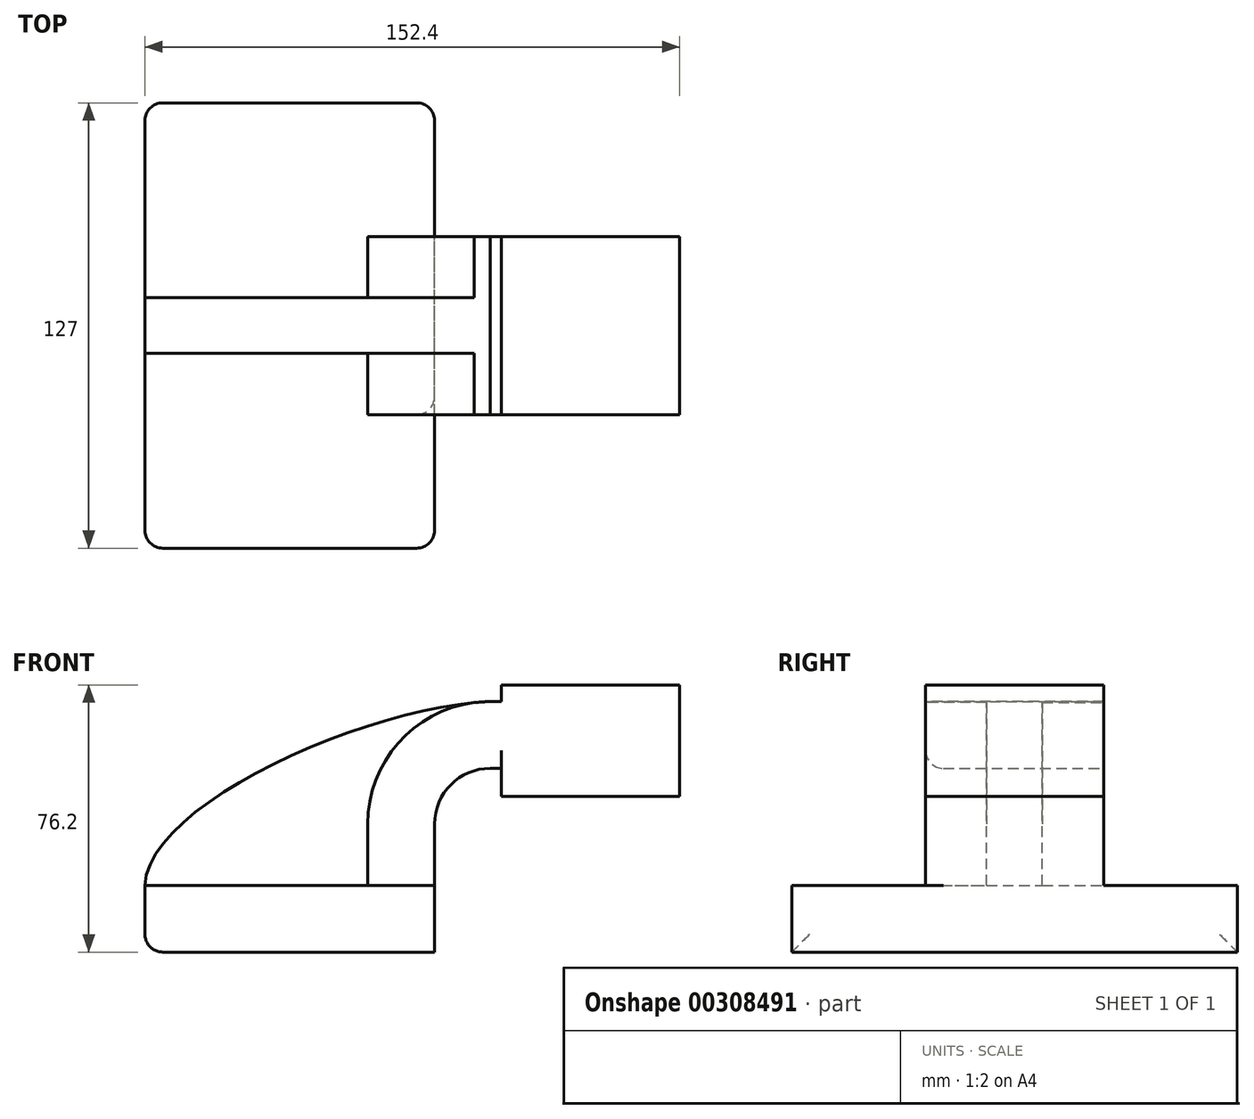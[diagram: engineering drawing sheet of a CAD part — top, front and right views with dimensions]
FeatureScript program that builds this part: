
annotation { "Feature Type Name" : "Feature", "Feature Type Description" : "" }
export const myFeature = defineFeature(function(context is Context, id is Id, definition is map)
    precondition{}
    {
        {
            var Q0;
            Q0=qCreatedBy(makeId("Front.planeOp"),FACE);
            var sketch = newSketch(context, id + "F0", { "sketchPlane" : qUnion([Q0])});
            skLineSegment(sketch, "E0.bottom", {"start": v(41.28, -9.52) * mm, "end": v(-41.28, -9.53) * mm});
            skLineSegment(sketch, "E0.top", {"start": v(41.27, 9.53) * mm, "end": v(-41.28, 9.53) * mm});
            skLineSegment(sketch, "E0.left", {"start": v(41.28, -9.52) * mm, "end": v(41.28, 9.53) * mm});
            skLineSegment(sketch, "E0.right", {"start": v(-41.28, -9.53) * mm, "end": v(-41.28, 9.53) * mm});
            skPoint(sketch, "E0.middle", {"position": v(0, 0) * mm});
            skLineSegment(sketch, "E1.bottom", {"start": v(60.32, 34.93) * mm, "end": v(111.12, 34.93) * mm});
            skLineSegment(sketch, "E1.top", {"start": v(60.32, 66.68) * mm, "end": v(111.12, 66.68) * mm});
            skLineSegment(sketch, "E1.left", {"start": v(60.32, 34.93) * mm, "end": v(60.32, 66.68) * mm});
            skLineSegment(sketch, "E1.right", {"start": v(111.12, 34.93) * mm, "end": v(111.12, 66.68) * mm});
            skPoint(sketch, "E1.middle", {"position": v(85.72, 50.8) * mm});
            skLineSegment(sketch, "E2", {"start": v(41.27, 9.53) * mm, "end": v(41.27, 27) * mm});
            skArc(sketch, "E3", {"start": v(41.27, 27) * mm, "mid": v(45.92, 38.23) * mm, "end": v(57.15, 42.88) * mm});
            skLineSegment(sketch, "E4", {"start": v(57.15, 42.88) * mm, "end": v(110.29, 42.88) * mm});
            skLineSegment(sketch, "E5.0", {"start": v(57.15, 61.93) * mm, "end": v(110.29, 61.93) * mm});
            skArc(sketch, "E5.1", {"start": v(22.23, 27) * mm, "mid": v(32.45, 51.7) * mm, "end": v(57.15, 61.93) * mm});
            skLineSegment(sketch, "E5.2", {"start": v(22.23, 9.53) * mm, "end": v(22.23, 27) * mm});
            skLineSegment(sketch, "E6", {"start": v(110.29, 42.88) * mm, "end": v(110.29, 61.93) * mm});
            skFitSpline(sketch, "E7", {"points": [v(-41.28, 9.53) * mm, v(57.15, 61.93) * mm], "startDerivative": vector(2.65, 70.47) * mm, "endDerivative": vector(102.94, 3.6) * mm});
            skLineSegment(sketch, "E8", {"start": v(111.12, 66.68) * mm, "end": v(111.12, 34.93) * mm});
            skSolve(sketch);
        }
        {
            var Q0;
            Q0=makeQuery(id+"F0.imprint","IMPRINT",FACE,{"disambiguationData":[TD([[makeQuery(id+"F0.imprint","IMPRINT",EDGE,{"derivedFrom":sQuery(id+"F0.wireOp",EDGE,"E0.bottom")}),-1.0]])]});
            extrude(context, id + "F1", {"entities" : qUnion([Q0]), "endBound" : BoundingType.SYMMETRIC, "depth" : 127 * mm});
        }
        {
            var Q0;
            {var subQ1=sQuery(id+"F0.wireOp",EDGE,"E2");Q0=makeQuery(id+"F0.imprint","IMPRINT",FACE,{"disambiguationData":[TD([[makeQuery(id+"F0.imprint","IMPRINT",EDGE,{"derivedFrom":subQ1}),1.0]])]});}
            var Q1;
            {var subQ5=sQuery(id+"F0.wireOp",EDGE,"E6");Q1=makeQuery(id+"F0.imprint","IMPRINT",FACE,{"disambiguationData":[TD([[makeQuery(id+"F0.imprint","IMPRINT",EDGE,{"derivedFrom":subQ5}),1.0]])]});}
            var Q2;
            {var subQ5=sQuery(id+"F0.wireOp",EDGE,"E1.bottom");Q2=makeQuery(id+"F0.imprint","IMPRINT",FACE,{"disambiguationData":[TD([[makeQuery(id+"F0.imprint","IMPRINT",EDGE,{"derivedFrom":subQ5}),1.0]])]});}
            extrude(context, id + "F2", {"entities" : qUnion([Q0, Q1, Q2]), "operationType" : NewBodyOperationType.ADD, "endBound" : BoundingType.SYMMETRIC, "depth" : 50.8 * mm});
        }
        {
            var Q0;
            {var subQ3=sQuery(id+"F0.wireOp",EDGE,"E5.2");Q0=makeQuery(id+"F0.imprint","IMPRINT",FACE,{"disambiguationData":[TD([[makeQuery(id+"F0.imprint","IMPRINT",EDGE,{"derivedFrom":subQ3}),1.0]])]});}
            extrude(context, id + "F3", {"entities" : qUnion([Q0]), "operationType" : NewBodyOperationType.ADD, "endBound" : BoundingType.SYMMETRIC, "depth" : 15.88 * mm});
        }
        {
            var Q0;
            Q0=makeQuery(id+"F1.opExtrude","CAP_EDGE",EDGE,{"disambiguationData":[OSD([sQuery(id+"F0.wireOp",EDGE,"E0.left")])],"isStart":false});
            var Q1;
            Q1=makeQuery(id+"F1.opExtrude","CAP_EDGE",EDGE,{"disambiguationData":[OSD([sQuery(id+"F0.wireOp",EDGE,"E0.left")])],"isStart":true});
            var Q2;
            Q2=makeQuery(id+"F2.opExtrude","CAP_EDGE",EDGE,{"disambiguationData":[OSD([sQuery(id+"F0.wireOp",EDGE,"E4")])],"isStart":false});
            var Q3;
            Q3=makeQuery(id+"F1.opExtrude","CAP_EDGE",EDGE,{"disambiguationData":[OSD([sQuery(id+"F0.wireOp",EDGE,"E0.right")])],"isStart":false});
            var Q4;
            Q4=makeQuery(id+"F1.opExtrude","CAP_EDGE",EDGE,{"disambiguationData":[OSD([sQuery(id+"F0.wireOp",EDGE,"E0.right")])],"isStart":true});
            var Q5;
            Q5=makeQuery(id+"F1.opExtrude","SWEPT_EDGE",EDGE,{"disambiguationData":[OSD([sQuery(id+"F0.wireOp",EDGE,"E0.bottom"),sQuery(id+"F0.wireOp",EDGE,"E0.right")])]});
            fillet(context, id + "F4", {"entities" : qUnion([Q0, Q1, Q2, Q3, Q4, Q5]), "radius" : 5.08 * mm, "tangentPropagation" : true, "allowEdgeOverflow" : false});
        }
    });
